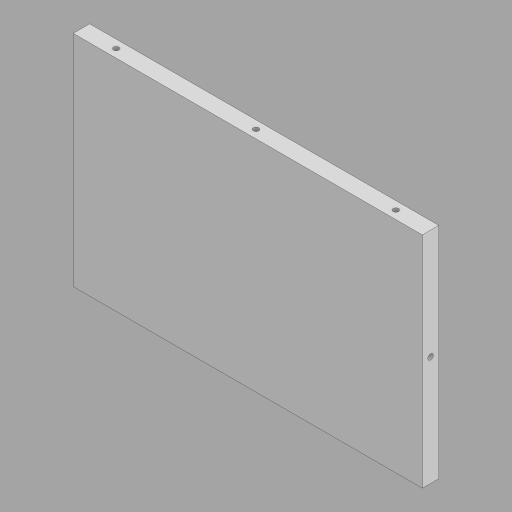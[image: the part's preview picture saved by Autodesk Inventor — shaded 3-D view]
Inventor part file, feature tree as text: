
AUTODESK INVENTOR PART (.ipt)
format: ipt  version: 2023.2 (Build 272271030, 271C)  size: 251,392 bytes
history: native  units: mm
features: extrude x4, sketch x3, projected_geometry x2
ambient origin geometry x8: Origin, YZ Plane, XZ Plane, XY Plane, X Axis, Y Axis, Z Axis, Center Point
bodies: Solid1 (feature_tree)
feature tree (9):
  extrude  "Extrusion1"  Depth=120.0mm
  extrude  "Extrusion2"  Depth=9.0mm
  extrude  "Extrusion3"  Depth=10.0mm
  extrude  "Extrusion4"  Depth=10.0mm TaperAngle=0.0deg
  sketch  "Sketch1"  dims[d0=191.0mm d1=120.0mm]
  sketch  "Sketch2"  dims[d2=9.0mm d3=0.0mm d4=3.0mm]
  projected_geometry  "Projected Loop1"
  sketch  "Sketch4"  dims[d5=3.0mm d6=3.0mm d7=10.0mm d8=0.0mm d9=10.0mm d10=0.0mm d11=3.0mm d12=10.0mm d13=0.0mm d15=3.0mm d17=76.5mm d18=76.5mm]
  projected_geometry  "Projected Loop2"
